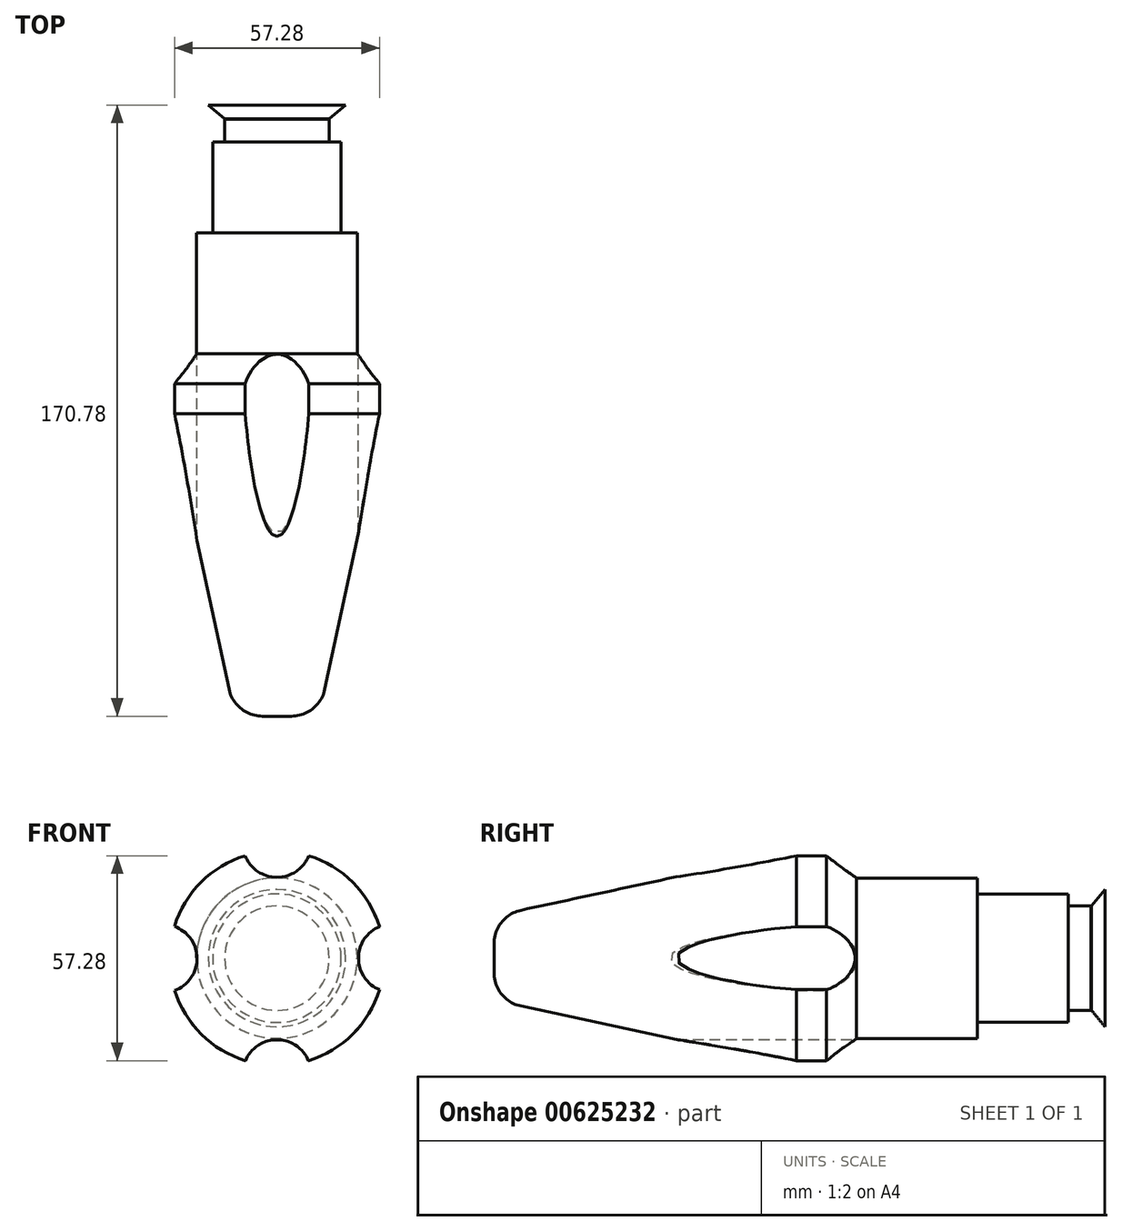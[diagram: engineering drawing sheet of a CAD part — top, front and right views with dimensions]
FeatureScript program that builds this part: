
annotation { "Feature Type Name" : "Feature", "Feature Type Description" : "" }
export const myFeature = defineFeature(function(context is Context, id is Id, definition is map)
    precondition{}
    {
        {
            var Q0;
            Q0=qCreatedBy(makeId("Front.planeOp"),FACE);
            var sketch = newSketch(context, id + "F0", { "sketchPlane" : qUnion([Q0])});
            skCircle(sketch, "E0", {"center": v(0, 0) * mm, "radius": 29.97 * mm});
            skSolve(sketch);
        }
        {
            var Q0;
            Q0=makeQuery(id+"F0.imprint","IMPRINT",FACE,{"disambiguationData":[TD([[makeQuery(id+"F0.imprint","IMPRINT",EDGE,{"derivedFrom":sQuery(id+"F0.wireOp",EDGE,"E0")}),1.0]])]});
            extrude(context, id + "F1", {"entities" : qUnion([Q0]), "depth" : 8.38 * mm, "offsetDistance" : 25.4 * mm});
        }
        {
            var Q0;
            Q0=qCreatedBy(makeId("Right.planeOp"),FACE);
            var sketch = newSketch(context, id + "F2", { "sketchPlane" : qUnion([Q0])});
            skLineSegment(sketch, "E1", {"start": v(0, 0) * mm, "end": v(8.38, 0) * mm});
            skLineSegment(sketch, "E2", {"start": v(8.38, 0) * mm, "end": v(8.38, 22.42) * mm});
            skLineSegment(sketch, "E3", {"start": v(8.38, 22.42) * mm, "end": v(0, 29.97) * mm});
            skLineSegment(sketch, "E4", {"start": v(0, 29.97) * mm, "end": v(0, 0) * mm});
            skSolve(sketch);
        }
        {
            var Q0;
            Q0=makeQuery(id+"F2.imprint","IMPRINT",FACE,{"disambiguationData":[TD([[makeQuery(id+"F2.imprint","IMPRINT",EDGE,{"derivedFrom":sQuery(id+"F2.wireOp",EDGE,"E1")}),1.0]])]});
            var Q1;
            Q1=sQuery(id+"F2.wireOp",EDGE,"E1");
            revolve(context, id + "F3", {"operationType" : NewBodyOperationType.ADD, "entities" : qUnion([Q0]), "axis" : qUnion([Q1]), "revolveType" : RevolveType.FULL});
        }
        {
            var Q0;
            Q0=qCreatedBy(makeId("Right.planeOp"),FACE);
            var sketch = newSketch(context, id + "F4", { "sketchPlane" : qUnion([Q0])});
            skLineSegment(sketch, "E5", {"start": v(-8.36, 0) * mm, "end": v(-92.94, 0) * mm});
            skLineSegment(sketch, "E6", {"start": v(-92.94, 0) * mm, "end": v(-92.94, 4.08) * mm});
            skLineSegment(sketch, "E7", {"start": v(-85.42, 13.39) * mm, "end": v(-8.36, 29.97) * mm});
            skLineSegment(sketch, "E8", {"start": v(-8.36, 29.97) * mm, "end": v(-8.36, 0) * mm});
            skPoint(sketch, "E9.visualSharp", {"position": v(-92.94, 11.77) * mm});
            skArc(sketch, "E9.filletArc", {"start": v(-85.42, 13.39) * mm, "mid": v(-90.83, 10.06) * mm, "end": v(-92.94, 4.08) * mm});
            skSolve(sketch);
        }
        {
            var Q0;
            Q0=makeQuery(id+"F4.imprint","IMPRINT",FACE,{"disambiguationData":[TD([[makeQuery(id+"F4.imprint","IMPRINT",EDGE,{"derivedFrom":sQuery(id+"F4.wireOp",EDGE,"E5")}),-1.0]])]});
            var Q1;
            Q1=sQuery(id+"F4.wireOp",EDGE,"E5");
            revolve(context, id + "F5", {"operationType" : NewBodyOperationType.ADD, "entities" : qUnion([Q0]), "axis" : qUnion([Q1]), "revolveType" : RevolveType.FULL});
        }
        {
            var Q0;
            Q0=qCreatedBy(makeId("Front.planeOp"),FACE);
            var sketch = newSketch(context, id + "F6", { "sketchPlane" : qUnion([Q0])});
            skCircle(sketch, "E10", {"center": v(0, 32.1) * mm, "radius": 9.53 * mm});
            skCircle(sketch, "E11", {"center": v(-31.85, -0.1) * mm, "radius": 9.53 * mm});
            skCircle(sketch, "E12", {"center": v(0, -32.27) * mm, "radius": 9.53 * mm});
            skCircle(sketch, "E13", {"center": v(32.27, 0) * mm, "radius": 9.53 * mm});
            skSolve(sketch);
        }
        {
            var Q0;
            Q0=sQuery(id+"F6.wireOp",VERTEX,"E10.center");
            var Q1;
            Q1=sQuery(id+"F6.wireOp",VERTEX,"E13.center");
            var Q2;
            Q2=sQuery(id+"F6.wireOp",VERTEX,"E12.center");
            var Q3;
            Q3=sQuery(id+"F6.wireOp",VERTEX,"E11.center");
            var Q4;
            Q4=makeQuery(id+"F1.opExtrude","SWEPT_BODY",BODY,{"disambiguationData":[OSD([sQuery(id+"F0.wireOp",EDGE,"E0")])]});
            hole(context, id + "F7", {"style" : HoleStyle.SIMPLE, "endStyle" : HoleEndStyle.THROUGH, "oppositeDirection" : true, "holeDiameter" : 19.05 * mm, "majorDiameter" : 6.35 * mm, "isTappedThrough" : true, "tappedDepth" : 12.7 * mm, "tapClearance" : 3, "startFromSketch" : true, "locations" : qUnion([Q0, Q1, Q2, Q3]), "scope" : qUnion([Q4])});
        }
        {
            var Q0;
            Q0=sQuery(id+"F6.wireOp",VERTEX,"E10.center");
            var Q1;
            Q1=sQuery(id+"F6.wireOp",VERTEX,"E11.center");
            var Q2;
            Q2=sQuery(id+"F6.wireOp",VERTEX,"E12.center");
            var Q3;
            Q3=sQuery(id+"F6.wireOp",VERTEX,"E13.center");
            var Q4;
            Q4=makeQuery(id+"F1.opExtrude","SWEPT_BODY",BODY,{"disambiguationData":[OSD([sQuery(id+"F0.wireOp",EDGE,"E0")])]});
            hole(context, id + "F8", {"style" : HoleStyle.SIMPLE, "endStyle" : HoleEndStyle.BLIND, "holeDiameter" : 19.05 * mm, "majorDiameter" : 6.35 * mm, "holeDepth" : 8.38 * mm, "isTappedThrough" : true, "tappedDepth" : 12.7 * mm, "tapClearance" : 3, "startFromSketch" : true, "locations" : qUnion([Q0, Q1, Q2, Q3]), "scope" : qUnion([Q4])});
        }
        {
            var Q0;
            Q0=makeQuery(id+"F3.opRevolve","SWEPT_FACE",FACE,{"disambiguationData":[OSD([sQuery(id+"F2.wireOp",EDGE,"E2")])]});
            cPlane(context, id + "F9", {"entities" : qUnion([Q0]), "cplaneType" : CPlaneType.OFFSET, "offset" : 0 * mm, "width" : 152.4 * mm, "height" : 152.4 * mm});
        }
        {
            var Q0;
            Q0=qCreatedBy(id+"F9.planeOp",FACE);
            var sketch = newSketch(context, id + "F10", { "sketchPlane" : qUnion([Q0])});
            skCircle(sketch, "E14", {"center": v(0, 0) * mm, "radius": 22.42 * mm});
            skSolve(sketch);
        }
        {
            var Q0;
            Q0 = qSketchRegion(id + "F10", true);
            extrude(context, id + "F11", {"entities" : qUnion([Q0]), "operationType" : NewBodyOperationType.ADD, "depth" : 33.78 * mm, "offsetDistance" : 25.4 * mm});
        }
        {
            var Q0;
            Q0=makeQuery(id+"F11.opExtrude","CAP_FACE",FACE,{"disambiguationData":[OSD([sQuery(id+"F10.wireOp",EDGE,"E14")])],"isStart":false});
            cPlane(context, id + "F12", {"entities" : qUnion([Q0]), "cplaneType" : CPlaneType.OFFSET, "offset" : 0 * mm, "width" : 152.4 * mm, "height" : 152.4 * mm});
        }
        {
            var Q0;
            Q0=qCreatedBy(id+"F12.planeOp",FACE);
            var sketch = newSketch(context, id + "F13", { "sketchPlane" : qUnion([Q0])});
            skCircle(sketch, "E15", {"center": v(0, 0) * mm, "radius": 17.96 * mm});
            skSolve(sketch);
        }
        {
            var Q0;
            Q0 = qSketchRegion(id + "F13", true);
            var Q1;
            Q1=makeQuery(id+"F13.imprint","IMPRINT",FACE,{"disambiguationData":[TD([[makeQuery(id+"F13.imprint","IMPRINT",EDGE,{"derivedFrom":sQuery(id+"F13.wireOp",EDGE,"E15")}),1.0]])]});
            extrude(context, id + "F14", {"entities" : qUnion([Q0, Q1]), "operationType" : NewBodyOperationType.ADD, "depth" : 25.4 * mm, "offsetDistance" : 25.4 * mm});
        }
        {
            var Q0;
            Q0=makeQuery(id+"F14.opExtrude","CAP_FACE",FACE,{"disambiguationData":[OSD([sQuery(id+"F13.wireOp",EDGE,"E15")])],"isStart":false});
            cPlane(context, id + "F15", {"entities" : qUnion([Q0]), "cplaneType" : CPlaneType.OFFSET, "offset" : 0 * mm, "width" : 152.4 * mm, "height" : 152.4 * mm});
        }
        {
            var Q0;
            Q0=qCreatedBy(id+"F15.planeOp",FACE);
            var sketch = newSketch(context, id + "F16", { "sketchPlane" : qUnion([Q0])});
            skCircle(sketch, "E16", {"center": v(0, 0) * mm, "radius": 14.6 * mm});
            skSolve(sketch);
        }
        {
            var Q0;
            Q0 = qSketchRegion(id + "F16", true);
            extrude(context, id + "F17", {"entities" : qUnion([Q0]), "operationType" : NewBodyOperationType.ADD, "depth" : 6.35 * mm, "offsetDistance" : 25.4 * mm});
        }
        {
            var Q0;
            Q0=qCreatedBy(makeId("Right.planeOp"),FACE);
            var sketch = newSketch(context, id + "F18", { "sketchPlane" : qUnion([Q0])});
            skLineSegment(sketch, "E17", {"start": v(697.1, 0) * mm, "end": v(700.92, 0) * mm});
            skLineSegment(sketch, "E18", {"start": v(74.03, 0) * mm, "end": v(77.84, 0) * mm});
            skLineSegment(sketch, "E19", {"start": v(74.03, 0) * mm, "end": v(74.03, 14.6) * mm});
            skLineSegment(sketch, "E20", {"start": v(74.03, 14.6) * mm, "end": v(77.84, 19.2) * mm});
            skLineSegment(sketch, "E21", {"start": v(77.84, 19.2) * mm, "end": v(77.84, 0) * mm});
            skSolve(sketch);
        }
        {
            var Q0;
            Q0 = qSketchRegion(id + "F18", true);
            var Q1;
            Q1 = qBodyType(qCreatedBy(id + "F18" ,EDGE), BodyType.WIRE);
            var Q2;
            Q2=sQuery(id+"F18.wireOp",EDGE,"E21");
            var Q3;
            Q3=sQuery(id+"F18.wireOp",EDGE,"E18");
            revolve(context, id + "F19", {"surfaceOperationType" : NewSurfaceOperationType.NEW, "entities" : qUnion([Q0]), "surfaceEntities" : qUnion([Q1, Q2]), "axis" : qUnion([Q3]), "revolveType" : RevolveType.FULL});
        }
    });
